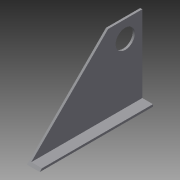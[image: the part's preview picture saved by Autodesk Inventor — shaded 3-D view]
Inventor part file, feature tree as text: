
AUTODESK INVENTOR PART (.ipt)
format: ipt  version: 2013 (Build 170138000, 138)  size: 92,160 bytes
history: native  units: in
note: dims shown in document units (in); Inventor stores cm internally (conversion verified against a paired STEP export)
features: extrude x2, sketch x2
ambient origin geometry x8: Origin, YZ Plane, XZ Plane, XY Plane, X Axis, Y Axis, Z Axis, Center Point
bodies: Solid1 (feature_tree)
feature tree (4):
  extrude  "Extrusion1"  TaperAngle=0.0deg  [1 undecoded]
  extrude  "Extrusion2"  Depth=1.0in
  sketch  "Sketch1"  dims[d0=3.625in d1=0.0in]
  sketch  "Sketch2"  dims[d2=1.125in d3=1.0in d4=0.0in d5=1.0in d6=90.0deg d7=1.0in d8=90.0deg d9=135.0deg d10=0.125in d11=0.0in d12=0.125in d13=90.0deg d14=0.625in d15=0.0in]
note: 1 required parameter value undecoded (feature->parameter linkage not recoverable at this tier; creation-order binding heuristic only, values carry confidence <= 0.55)
